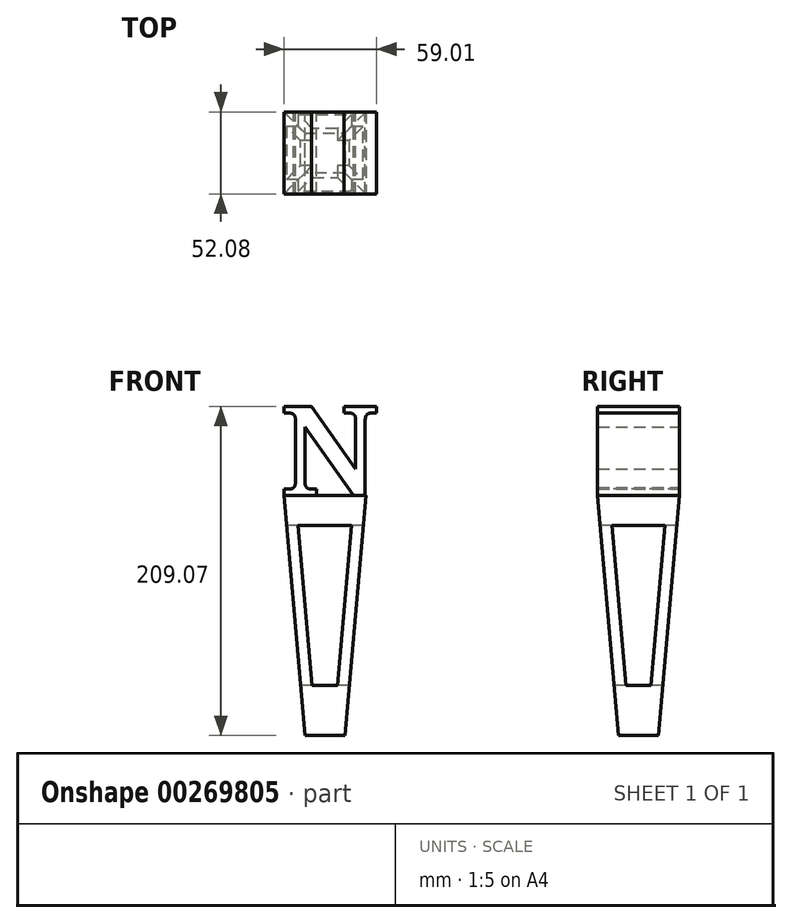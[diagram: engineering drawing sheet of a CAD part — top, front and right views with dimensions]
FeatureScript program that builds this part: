
annotation { "Feature Type Name" : "Feature", "Feature Type Description" : "" }
export const myFeature = defineFeature(function(context is Context, id is Id, definition is map)
    precondition{}
    {
        {
            var Q0;
            Q0=qCreatedBy(makeId("Top.planeOp"),FACE);
            var sketch = newSketch(context, id + "F0", { "sketchPlane" : qUnion([Q0])});
            skLineSegment(sketch, "E0.bottom", {"start": v(12.7, 12.7) * mm, "end": v(-12.7, 12.7) * mm});
            skLineSegment(sketch, "E0.top", {"start": v(12.7, -12.7) * mm, "end": v(-12.7, -12.7) * mm});
            skLineSegment(sketch, "E0.left", {"start": v(12.7, 12.7) * mm, "end": v(12.7, -12.7) * mm});
            skLineSegment(sketch, "E0.right", {"start": v(-12.7, 12.7) * mm, "end": v(-12.7, -12.7) * mm});
            skPoint(sketch, "E0.middle", {"position": v(0, 0) * mm});
            skSolve(sketch);
        }
        {
            var Q0;
            Q0=makeQuery(id+"F0.imprint","IMPRINT",FACE,{"disambiguationData":[TD([[makeQuery(id+"F0.imprint","IMPRINT",EDGE,{"derivedFrom":sQuery(id+"F0.wireOp",EDGE,"E0.bottom")}),1.0]])]});
            extrude(context, id + "F1", {"entities" : qUnion([Q0]), "depth" : 152.4 * mm, "offsetDistance" : 25.4 * mm, "hasDraft" : true, "draftAngle" : 5 * degree});
        }
        {
            var Q0;
            Q0=qCreatedBy(makeId("Right.planeOp"),FACE);
            var sketch = newSketch(context, id + "F2", { "sketchPlane" : qUnion([Q0])});
            skLineSegment(sketch, "E1", {"start": v(-7.98, 31.75) * mm, "end": v(-16.86, 133.35) * mm});
            skLineSegment(sketch, "E2", {"start": v(-16.86, 133.35) * mm, "end": v(16.86, 133.35) * mm});
            skLineSegment(sketch, "E3", {"start": v(16.86, 133.35) * mm, "end": v(7.98, 31.75) * mm});
            skLineSegment(sketch, "E4", {"start": v(7.98, 31.75) * mm, "end": v(-7.98, 31.75) * mm});
            skLineSegment(sketch, "E5", {"start": v(0, 0) * mm, "end": v(0, 31.75) * mm, "construction": true});
            skSolve(sketch);
        }
        {
            var Q0;
            Q0 = qSketchRegion(id + "F2", true);
            var Q1;
            Q1=makeQuery(id+"F1.opExtrude","SWEPT_FACE",FACE,{"disambiguationData":[OSD([sQuery(id+"F0.wireOp",EDGE,"E0.left")])]});
            var Q2;
            Q2=makeQuery(id+"F1.opExtrude","SWEPT_FACE",FACE,{"disambiguationData":[OSD([sQuery(id+"F0.wireOp",EDGE,"E0.right")])]});
            extrude(context, id + "F3", {"entities" : qUnion([Q0]), "operationType" : NewBodyOperationType.REMOVE, "endBound" : BoundingType.UP_TO_SURFACE, "depth" : 25.4 * mm, "endBoundEntityFace" : qUnion([Q1]), "offsetDistance" : 25.4 * mm, "hasSecondDirection" : true, "secondDirectionBound" : SecondDirectionBoundingType.UP_TO_SURFACE, "secondDirectionOppositeDirection" : true, "secondDirectionDepth" : 25.4 * mm, "secondDirectionBoundEntityFace" : qUnion([Q2])});
        }
        {
            var Q0;
            Q0=qCreatedBy(makeId("Front.planeOp"),FACE);
            var sketch = newSketch(context, id + "F4", { "sketchPlane" : qUnion([Q0])});
            skLineSegment(sketch, "E6", {"start": v(0, 0) * mm, "end": v(0, 31.75) * mm, "construction": true});
            skLineSegment(sketch, "E7", {"start": v(0, 31.75) * mm, "end": v(-7.98, 31.75) * mm});
            skLineSegment(sketch, "E8", {"start": v(-7.98, 31.75) * mm, "end": v(-16.86, 133.35) * mm});
            skLineSegment(sketch, "E9", {"start": v(-16.86, 133.35) * mm, "end": v(16.86, 133.35) * mm});
            skLineSegment(sketch, "E10", {"start": v(16.86, 133.35) * mm, "end": v(7.98, 31.75) * mm});
            skLineSegment(sketch, "E11", {"start": v(7.98, 31.75) * mm, "end": v(0, 31.75) * mm});
            skSolve(sketch);
        }
        {
            var Q0;
            Q0 = qSketchRegion(id + "F4", true);
            var Q1;
            Q1=makeQuery(id+"F1.opExtrude","SWEPT_FACE",FACE,{"disambiguationData":[OSD([sQuery(id+"F0.wireOp",EDGE,"E0.bottom")])]});
            var Q2;
            Q2=makeQuery(id+"F1.opExtrude","SWEPT_FACE",FACE,{"disambiguationData":[OSD([sQuery(id+"F0.wireOp",EDGE,"E0.top")])]});
            extrude(context, id + "F5", {"entities" : qUnion([Q0]), "operationType" : NewBodyOperationType.REMOVE, "endBound" : BoundingType.UP_TO_SURFACE, "oppositeDirection" : true, "depth" : 25.4 * mm, "endBoundEntityFace" : qUnion([Q1]), "offsetDistance" : 25.4 * mm, "hasSecondDirection" : true, "secondDirectionBound" : SecondDirectionBoundingType.UP_TO_SURFACE, "secondDirectionOppositeDirection" : false, "secondDirectionDepth" : 25.4 * mm, "secondDirectionBoundEntityFace" : qUnion([Q2])});
        }
        {
            var Q0;
            Q0=qCreatedBy(makeId("Front.planeOp"),FACE);
            var sketch = newSketch(context, id + "F6", { "sketchPlane" : qUnion([Q0])});
            skText(sketch, "E12", { "text": "N", "fontName": "NotoSerif-Bold.ttf"});
            const initialGuessF6  = {"E12": [-0.02821, 0.1524, 1, 0, 0.05715]};
            skSetInitialGuess(sketch, initialGuessF6);
            skSolve(sketch);
        }
        {
            var Q0;
            Q0 = qSketchRegion(id + "F6", true);
            extrude(context, id + "F7", {"entities" : qUnion([Q0]), "operationType" : NewBodyOperationType.ADD, "depth" : 26.03 * mm, "offsetDistance" : 25.4 * mm, "hasSecondDirection" : true, "secondDirectionOppositeDirection" : true, "secondDirectionDepth" : 26.03 * mm});
        }
    });
